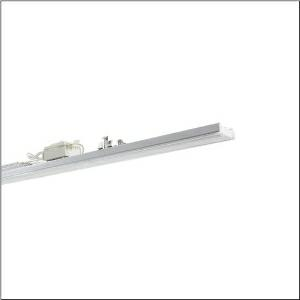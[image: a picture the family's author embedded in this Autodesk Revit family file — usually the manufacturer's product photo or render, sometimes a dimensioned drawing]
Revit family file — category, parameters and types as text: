
# Revit family: licross_11_recessed_mo_51te18mn495g
name_source: partatom
category: Lighting Fixtures
units: mm (PartAtom-declared; Revit-internal decimal feet)

## family parameters
Cut with Voids When Loaded = No
Host = Face
Light Source = No
Part Type = Normal
Room Calculation Point = No
Round Connector Dimension = Use Diameter
Shared = No

## types (1)
- --- (1 x LED, 9990 lm, 55.2 W, 4000K)
    Apparent Load = 55 VA
    CIE Flux Codes = 83 96 99 100 100
    Color Rendering = 80
    Color Temperature = 4000K
    Default Elevation = 1800 mm
    Description = Licross 11 Recessed MO, luminaire insert, of sheet steel, galvanised, coil coated, white, length: 1.500mm, width: 66mm, height: 67mm, LED rated luminous flux: 9.990lm, light colour: 840, SDCM (Standard Deviation of Colour Matching)MacAdam ≤ 2 SDCM (initial), control gear: ON/OFF Multilumen, with plug, 3-pole, with phase selection, mains connection: 220..240V, AC, 50/60Hz, rated input power: 55W, internal wiring halogen-free, primary light control with lens, of plastic, primary optical cover: cover, of PMMA, light emission: direct distribution, primary light characteristic: symmetric, protection rating (complete): IP54, insulation class (complete): insulation class I (protective earthing), certification: CE, ENEC, VDE, UKCA, protection symbol: D if used in an environment with non-conductive dust loads with corresponding accessories, impact resistance: IK06, permissible ambient temperature for indoor applications: -35..+40°C, corresponds to IFS (International Featured Standards) requirements for safety and quality in the food industry, reducing of maximum allowable ambient temperature of 5°C with ceiling mounting, The light source and the operating device comply with the requirements of the Ecodesign Regulation (EU) 2019/2020 and are replaceable in accordance with this regulation, packaging unit: 1 piece
    Height = 58 mm
    Lamp = 1 x LED
    Lamp Light Flux = 9990 lm
    Lamp Power = 55.2 W
    Lamp count = 1
    Length = 1500 mm
    Luminous efficacy = 181 lm/W
    Manufacturer = Siteco
    ModVariant = No
    Model = 51TE18MN495G
    Mounting Place = Ceiling
    Mounting Type = Pendant
    Number of Poles = 1
    OnlyDefault = Yes
    Power Factor = 1
    Product Name = Licross 11 Recessed MO
    Product group = luminaire insert | ceiling pendant
    ProductGroupID = 901
    Protection Class = Protection class I
    Protection Degree = IP 54
    RLX_Detail_Level = 1
    RLX_Emergency_Light_Flux = 0 lm
    RLX_Emergency_Type = 0
    RLX_Emergency_Type_DB = No
    RlxData = <blob elided: 22425 chars, md5=f1111d18>
    Socket = socket
    Standby Power = 0 W
    System Light Flux = 9990 lm
    System Power = 55 W
    Type Comments = factory setting: luminous flux: 100 % | (A | C | E) | 126 mA
    Type Image = l_1296930.jpg
    URL = http://relux.com
    VarID = @adj_089517
    Voltage = 0 V
    Weight = 0.00 kg
    Width = 66 mm

## geometry (parser evidence)
native form markers: Blend x4, Sweep x11
no freeform markers — native parametric forms only
